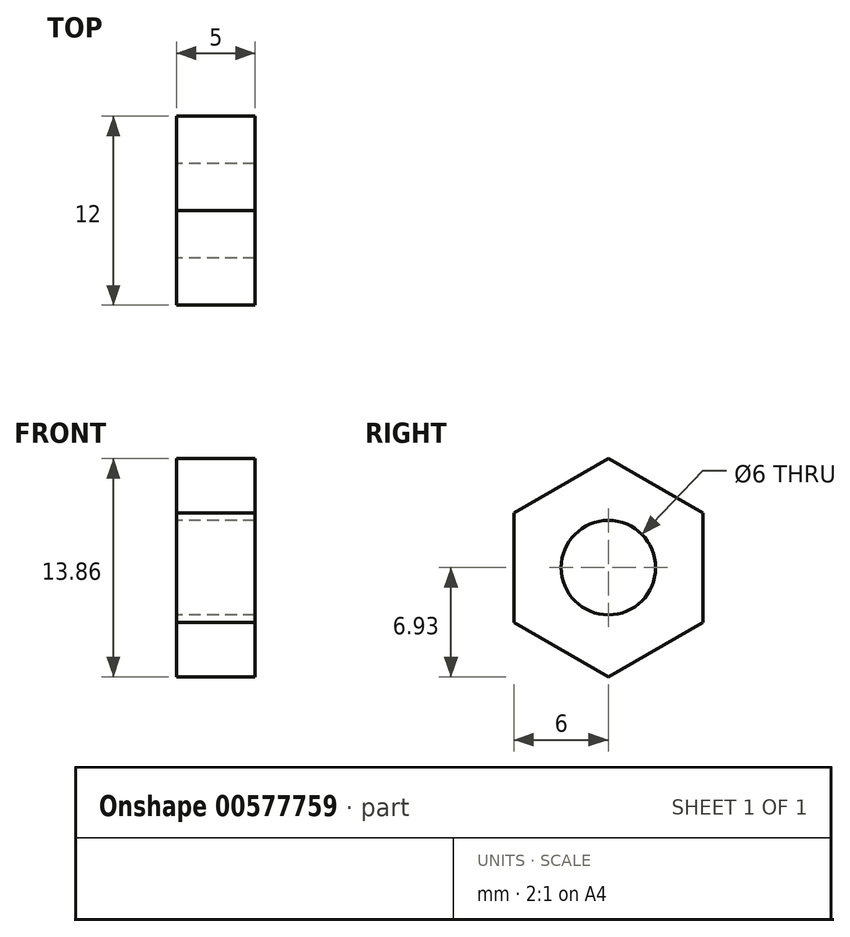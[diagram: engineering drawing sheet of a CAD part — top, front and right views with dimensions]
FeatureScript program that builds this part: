
annotation { "Feature Type Name" : "Feature", "Feature Type Description" : "" }
export const myFeature = defineFeature(function(context is Context, id is Id, definition is map)
    precondition{}
    {
        {
            var Q0;
            Q0=qCreatedBy(makeId("Right.planeOp"),FACE);
            var sketch = newSketch(context, id + "F0", { "sketchPlane" : qUnion([Q0])});
            skCircle(sketch, "E0", {"center": v(0, 0) * mm, "radius": 3 * mm});
            skCircle(sketch, "E1.cCircle", {"center": v(0, 0) * mm, "radius": 6 * mm, "construction": true});
            skLineSegment(sketch, "E1.0", {"start": v(6, -3.46) * mm, "end": v(0, -6.93) * mm});
            skLineSegment(sketch, "E1.1", {"start": v(0, -6.93) * mm, "end": v(-6, -3.46) * mm});
            skLineSegment(sketch, "E1.2", {"start": v(-6, -3.46) * mm, "end": v(-6, 3.46) * mm});
            skLineSegment(sketch, "E1.3", {"start": v(-6, 3.46) * mm, "end": v(0, 6.93) * mm});
            skLineSegment(sketch, "E1.4", {"start": v(0, 6.93) * mm, "end": v(6, 3.46) * mm});
            skLineSegment(sketch, "E1.5", {"start": v(6, 3.46) * mm, "end": v(6, -3.46) * mm});
            skPoint(sketch, "E1.0.midPoint", {"position": v(3, -5.2) * mm});
            skSolve(sketch);
        }
        {
            var Q0;
            Q0 = qSketchRegion(id + "F0", true);
            extrude(context, id + "F1", {"entities" : qUnion([Q0]), "depth" : 5 * mm, "offsetDistance" : 25 * mm});
        }
    });
